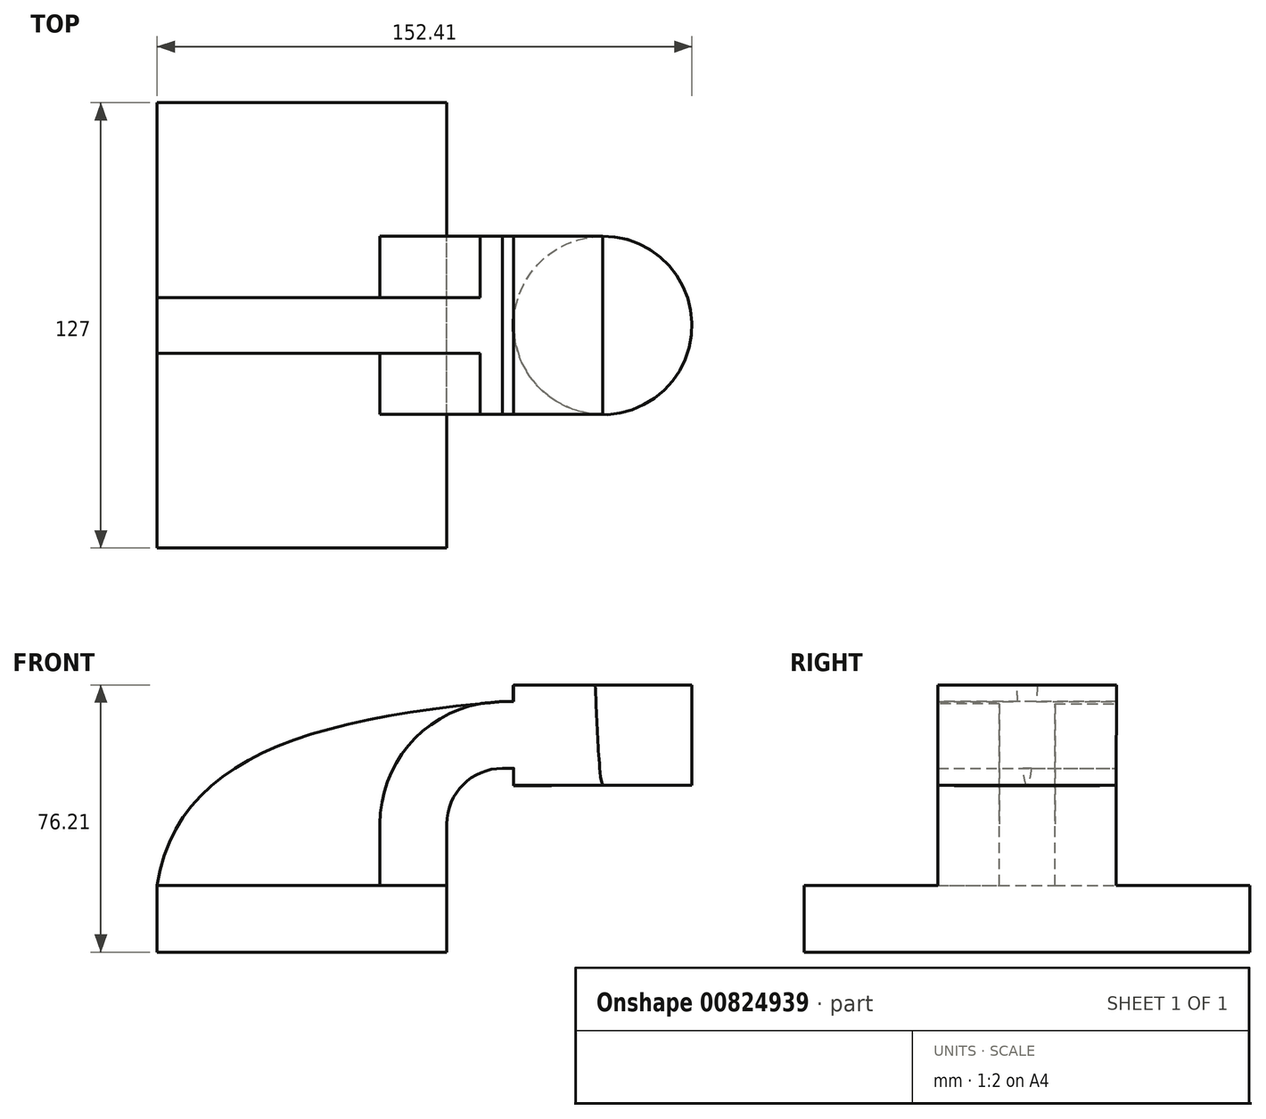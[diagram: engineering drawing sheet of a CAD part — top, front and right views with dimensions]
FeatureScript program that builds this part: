
annotation { "Feature Type Name" : "Feature", "Feature Type Description" : "" }
export const myFeature = defineFeature(function(context is Context, id is Id, definition is map)
    precondition{}
    {
        {
            var Q0;
            Q0=qCreatedBy(makeId("Front.planeOp"),FACE);
            var sketch = newSketch(context, id + "F0", { "sketchPlane" : qUnion([Q0])});
            skLineSegment(sketch, "E0.bottom", {"start": v(41.28, -9.52) * mm, "end": v(-41.27, -9.53) * mm});
            skLineSegment(sketch, "E0.top", {"start": v(41.27, 9.53) * mm, "end": v(-41.28, 9.53) * mm});
            skLineSegment(sketch, "E0.left", {"start": v(41.28, -9.52) * mm, "end": v(41.28, 9.53) * mm});
            skLineSegment(sketch, "E0.right", {"start": v(-41.27, -9.53) * mm, "end": v(-41.28, 9.53) * mm});
            skPoint(sketch, "E0.middle", {"position": v(0, 0) * mm});
            skLineSegment(sketch, "E1.bottom", {"start": v(111.12, 38.1) * mm, "end": v(60.32, 38.1) * mm});
            skLineSegment(sketch, "E1.top", {"start": v(111.12, 66.68) * mm, "end": v(60.32, 66.68) * mm});
            skLineSegment(sketch, "E1.left", {"start": v(111.12, 38.1) * mm, "end": v(111.12, 66.68) * mm});
            skLineSegment(sketch, "E1.right", {"start": v(60.32, 38.1) * mm, "end": v(60.32, 66.68) * mm});
            skPoint(sketch, "E1.middle", {"position": v(85.72, 52.39) * mm});
            skLineSegment(sketch, "E2", {"start": v(41.27, 9.53) * mm, "end": v(41.27, 27) * mm});
            skArc(sketch, "E3", {"start": v(41.27, 27) * mm, "mid": v(45.92, 38.23) * mm, "end": v(57.15, 42.88) * mm});
            skLineSegment(sketch, "E4", {"start": v(57.15, 42.88) * mm, "end": v(85.64, 42.88) * mm});
            skLineSegment(sketch, "E5.0", {"start": v(57.15, 61.93) * mm, "end": v(85.64, 61.93) * mm});
            skArc(sketch, "E5.1", {"start": v(22.23, 27) * mm, "mid": v(32.45, 51.7) * mm, "end": v(57.15, 61.93) * mm});
            skLineSegment(sketch, "E5.2", {"start": v(22.23, 9.53) * mm, "end": v(22.23, 27) * mm});
            skLineSegment(sketch, "E6", {"start": v(85.72, 38.1) * mm, "end": v(85.64, 66.68) * mm});
            skFitSpline(sketch, "E7", {"points": [v(-41.28, 9.53) * mm, v(57.15, 61.93) * mm], "startDerivative": vector(16.88, 106.45) * mm, "endDerivative": vector(171.45, 14.9) * mm});
            skSolve(sketch);
        }
        {
            var Q0;
            Q0=makeQuery(id+"F0.imprint","IMPRINT",FACE,{"disambiguationData":[TD([[makeQuery(id+"F0.imprint","IMPRINT",EDGE,{"derivedFrom":sQuery(id+"F0.wireOp",EDGE,"E0.bottom")}),-1.0]])]});
            extrude(context, id + "F1", {"entities" : qUnion([Q0]), "endBound" : BoundingType.SYMMETRIC, "depth" : 127 * mm, "offsetDistance" : 25.4 * mm});
        }
        {
            var Q0;
            {var subQ1=sQuery(id+"F0.wireOp",EDGE,"E2");Q0=makeQuery(id+"F0.imprint","IMPRINT",FACE,{"disambiguationData":[TD([[makeQuery(id+"F0.imprint","IMPRINT",EDGE,{"derivedFrom":subQ1}),1.0]])]});}
            var Q1;
            {var subQ6=sQuery(id+"F0.wireOp",EDGE,"E6");Q1=makeQuery(id+"F0.imprint","IMPRINT",FACE,{"disambiguationData":[TD([[makeQuery(id+"F0.imprint","IMPRINT",EDGE,{"derivedFrom":subQ6}),1.0]])]});}
            extrude(context, id + "F2", {"entities" : qUnion([Q0, Q1]), "operationType" : NewBodyOperationType.ADD, "endBound" : BoundingType.SYMMETRIC, "depth" : 50.8 * mm, "offsetDistance" : 25.4 * mm});
        }
        {
            var Q0;
            {var subQ3=sQuery(id+"F0.wireOp",EDGE,"E5.2");Q0=makeQuery(id+"F0.imprint","IMPRINT",FACE,{"disambiguationData":[TD([[makeQuery(id+"F0.imprint","IMPRINT",EDGE,{"derivedFrom":subQ3}),1.0]])]});}
            extrude(context, id + "F3", {"entities" : qUnion([Q0]), "operationType" : NewBodyOperationType.ADD, "endBound" : BoundingType.SYMMETRIC, "depth" : 15.88 * mm, "offsetDistance" : 25.4 * mm});
        }
        {
            var Q0;
            {var subQ0=sQuery(id+"F0.wireOp",EDGE,"E1.left");Q0=makeQuery(id+"F0.imprint","IMPRINT",FACE,{"disambiguationData":[TD([[makeQuery(id+"F0.imprint","IMPRINT",EDGE,{"derivedFrom":subQ0}),1.0]])]});}
            var Q1;
            Q1=sQuery(id+"F0.wireOp",EDGE,"E6");
            revolve(context, id + "F4", {"operationType" : NewBodyOperationType.ADD, "surfaceOperationType" : NewSurfaceOperationType.NEW, "entities" : qUnion([Q0]), "axis" : qUnion([Q1]), "revolveType" : RevolveType.FULL});
        }
    });
